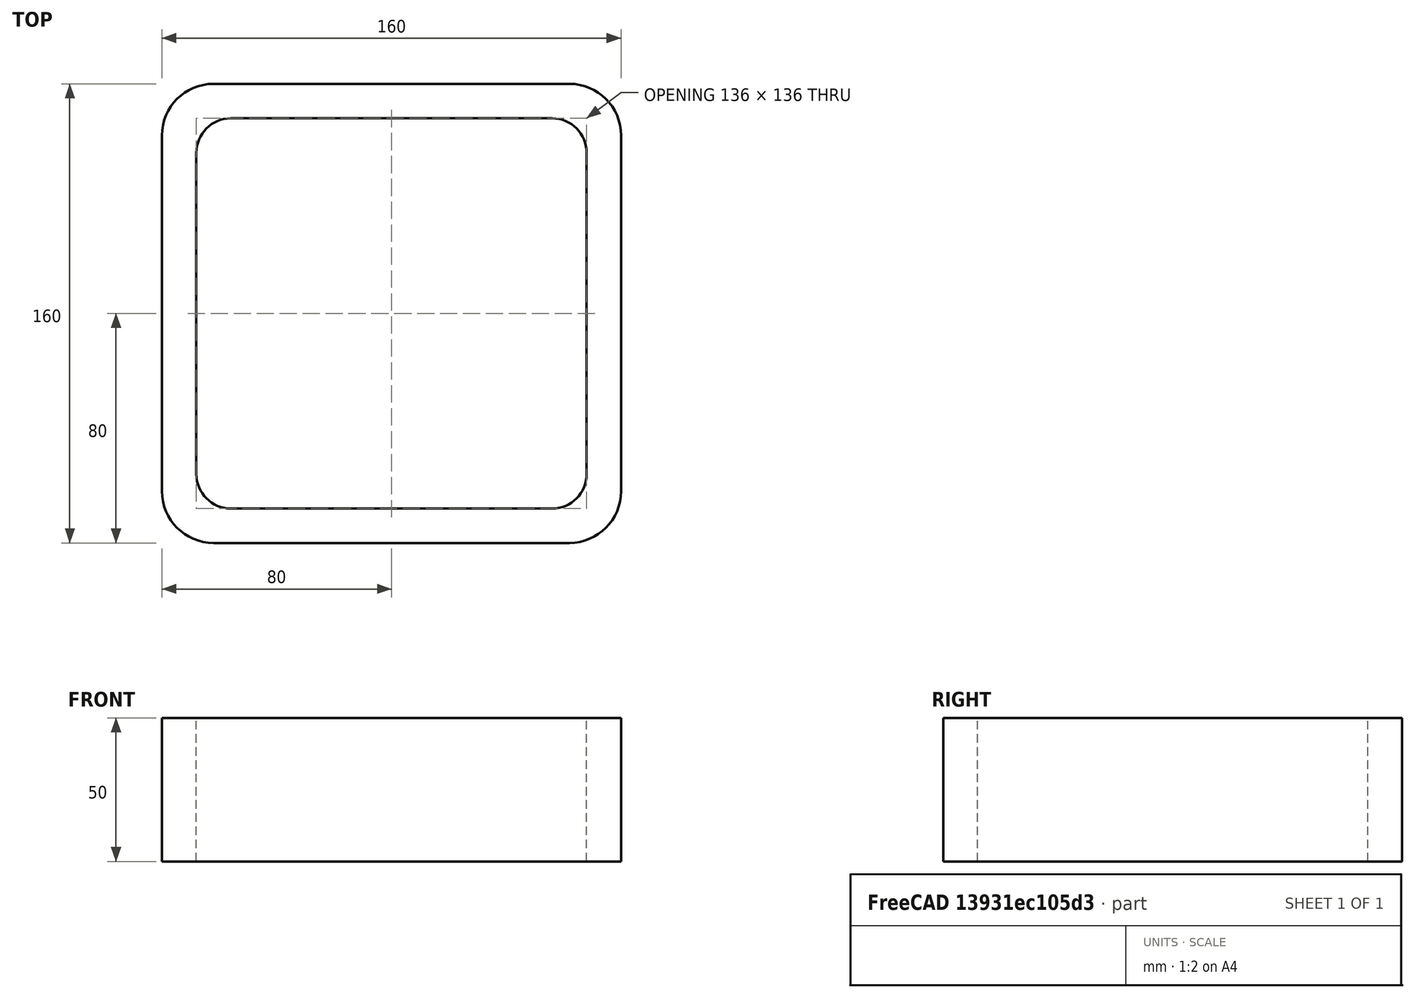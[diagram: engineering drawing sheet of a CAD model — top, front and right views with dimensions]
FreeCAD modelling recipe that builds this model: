
FCSTD DOCUMENT  (FreeCAD 0.15R4671 (Git))
Label: Square hollow section 160x160x12 EN10219 S235JRH
License: All rights reserved
LicenseURL: http://en.wikipedia.org/wiki/All_rights_reserved
objects: Sketcher::SketchObject×1, Part::Extrusion×1
note: 2 computed .brp shape members not serialized (recipe doc carries the construction recipe); baked Part::Feature solids carry a one-line shape summary decoded from their .brp

FEATURE [Sketcher::SketchObject] Sketch
  sketch-geometry (16):
    g0: LineSegment StartX=-56 StartY=68 StartZ=0 EndX=56 EndY=68 EndZ=0
    g1: LineSegment StartX=68 StartY=56 StartZ=0 EndX=68 EndY=-56 EndZ=0
    g2: LineSegment StartX=56 StartY=-68 StartZ=0 EndX=-56 EndY=-68 EndZ=0
    g3: LineSegment StartX=-68 StartY=-56 StartZ=0 EndX=-68 EndY=56 EndZ=0
    g4: LineSegment StartX=-62 StartY=80 StartZ=0 EndX=62 EndY=80 EndZ=0
    g5: LineSegment StartX=80 StartY=62 StartZ=0 EndX=80 EndY=-62 EndZ=0
    g6: LineSegment StartX=62 StartY=-80 StartZ=0 EndX=-62 EndY=-80 EndZ=0
    g7: LineSegment StartX=-80 StartY=-62 StartZ=0 EndX=-80 EndY=62 EndZ=0
    g8: ArcOfCircle CenterX=-56 CenterY=56 CenterZ=0 NormalX=0 NormalY=0 NormalZ=1 Radius=12 StartAngle=1.5708 EndAngle=3.14159
    g9: ArcOfCircle CenterX=56 CenterY=56 CenterZ=0 NormalX=0 NormalY=0 NormalZ=1 Radius=12 StartAngle=0 EndAngle=1.5708
    g10: ArcOfCircle CenterX=56 CenterY=-56 CenterZ=0 NormalX=0 NormalY=0 NormalZ=1 Radius=12 StartAngle=4.71239 EndAngle=6.28319
    g11: ArcOfCircle CenterX=-56 CenterY=-56 CenterZ=0 NormalX=0 NormalY=0 NormalZ=1 Radius=12 StartAngle=3.14159 EndAngle=4.71239
    g12: ArcOfCircle CenterX=62 CenterY=62 CenterZ=0 NormalX=0 NormalY=0 NormalZ=1 Radius=18 StartAngle=0 EndAngle=1.5708
    g13: ArcOfCircle CenterX=62 CenterY=-62 CenterZ=0 NormalX=0 NormalY=0 NormalZ=1 Radius=18 StartAngle=4.71239 EndAngle=6.28319
    g14: ArcOfCircle CenterX=-62 CenterY=-62 CenterZ=0 NormalX=0 NormalY=0 NormalZ=1 Radius=18 StartAngle=3.14159 EndAngle=4.71239
    g15: ArcOfCircle CenterX=-62 CenterY=62 CenterZ=0 NormalX=0 NormalY=0 NormalZ=1 Radius=18 StartAngle=1.5708 EndAngle=3.14159
  constraints (36):
    c: Horizontal(g2)
    c: Vertical(g3)
    c: Horizontal(g6)
    c: Vertical(g7)
    c: Tangent(g3,g8) = 1.5708
    c: Tangent(g0,g8) = 1.5708
    c: Tangent(g0,g9) = 1.5708
    c: Tangent(g1,g9) = 1.5708
    c: Tangent(g1,g10) = 1.5708
    c: Tangent(g2,g10) = 1.5708
    c: Tangent(g2,g11) = 1.5708
    c: Tangent(g3,g11) = 1.5708
    c: Tangent(g4,g12) = 1.5708
    c: Tangent(g5,g12) = 1.5708
    c: Tangent(g5,g13) = 1.5708
    c: Tangent(g6,g13) = 1.5708
    c: Tangent(g6,g14) = 1.5708
    c: Tangent(g7,g14) = 1.5708
    c: Tangent(g7,g15) = 1.5708
    c: Tangent(g4,g15) = 1.5708
    c: Equal(g9,g8)
    c: Equal(g9,g11)
    c: Equal(g9,g10)
    c: Equal(g12,g15)
    c: Equal(g12,g14)
    c: Equal(g12,g13)
    c: Symmetric(g4,g6,g-1)
    c: Symmetric(g7,g5,g-2)
    c: DistanceY(g4,g6) = -160
    c: DistanceX(g7,g5) = 160
    c: Symmetric(g3,g1,g-2)
    c: Symmetric(g0,g2,g-1)
    c: DistanceY(g0,g4) = 12
    c: DistanceX(g5,g1) = -12
    c: Radius(g9) = 12
    c: Radius(g12) = 18
FEATURE [Part::Extrusion] Extrude  label="Square hollow section 160x160x12 EN10219 S235JRH"
  Base = -> Sketch
  Dir = (0,0,50)
  Solid = true
